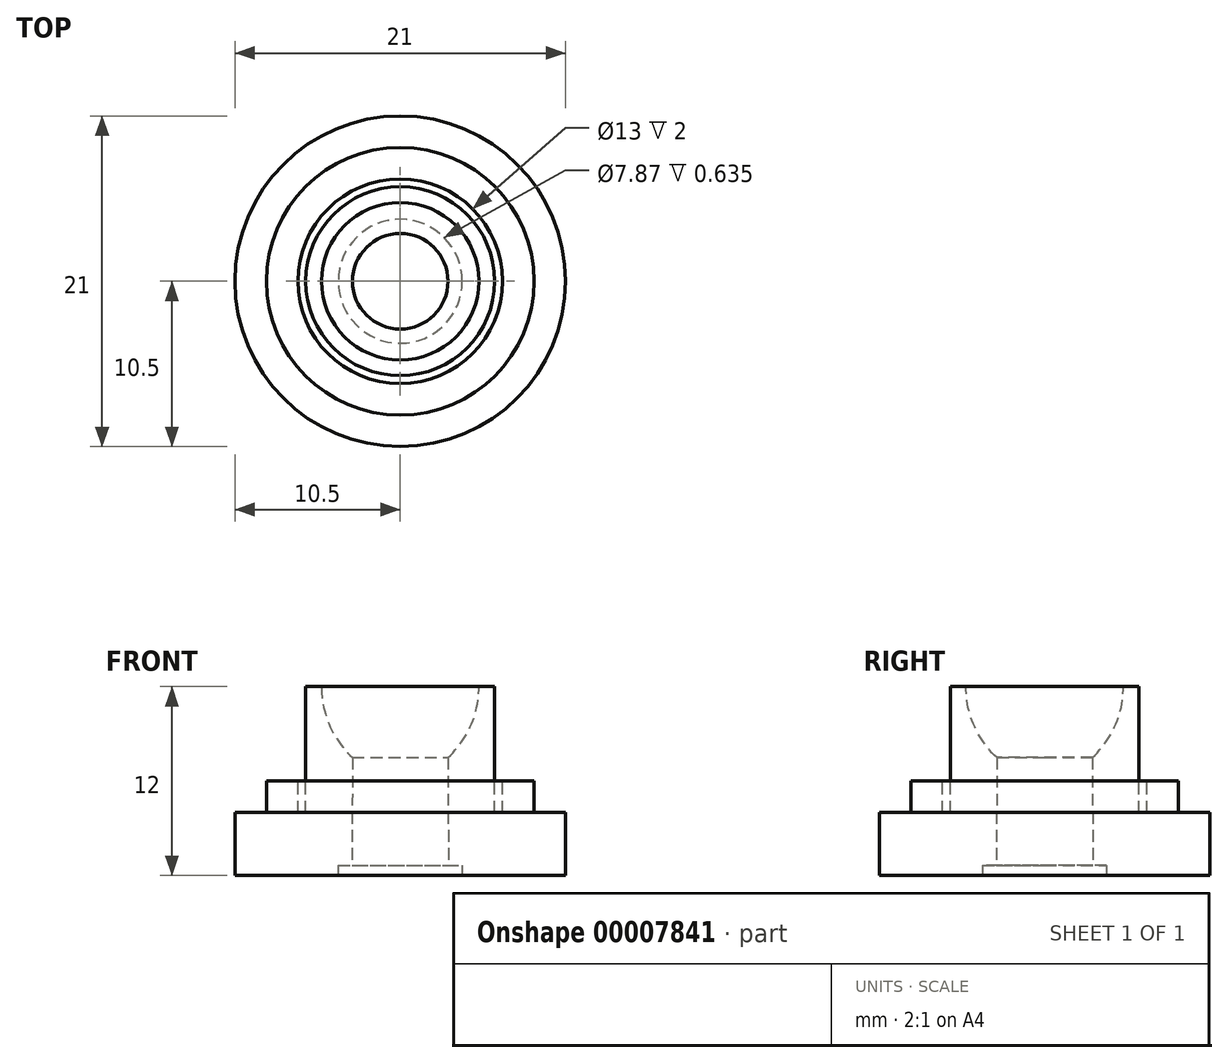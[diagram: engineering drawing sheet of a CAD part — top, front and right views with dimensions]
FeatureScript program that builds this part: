
annotation { "Feature Type Name" : "Feature", "Feature Type Description" : "" }
export const myFeature = defineFeature(function(context is Context, id is Id, definition is map)
    precondition{}
    {
        {
            var Q0;
            Q0=qCreatedBy(makeId("Right.planeOp"),FACE);
            var sketch = newSketch(context, id + "F0", { "sketchPlane" : qUnion([Q0])});
            skLineSegment(sketch, "E0", {"start": v(0, 39.52) * mm, "end": v(0, -33.2) * mm, "construction": true});
            skSolve(sketch);
        }
        {
            var Q0;
            Q0=qCreatedBy(makeId("Right.planeOp"),FACE);
            var sketch = newSketch(context, id + "F1", { "sketchPlane" : qUnion([Q0])});
            skLineSegment(sketch, "E1", {"start": v(0, 0) * mm, "end": v(3.94, 0) * mm});
            skLineSegment(sketch, "E2", {"start": v(3.94, 0) * mm, "end": v(3.94, 0.63) * mm});
            skLineSegment(sketch, "E3", {"start": v(3.94, 0.63) * mm, "end": v(3.06, 0.63) * mm});
            skLineSegment(sketch, "E4", {"start": v(3.06, 0.64) * mm, "end": v(3.04, 7.5) * mm});
            skLineSegment(sketch, "E5", {"start": v(3.04, 7.5) * mm, "end": v(0, 7.5) * mm});
            skLineSegment(sketch, "E6", {"start": v(0, 7.5) * mm, "end": v(0, 0) * mm});
            skSolve(sketch);
        }
        {
            var Q0;
            Q0=qCreatedBy(makeId("Right.planeOp"),FACE);
            var sketch = newSketch(context, id + "F2", { "sketchPlane" : qUnion([Q0])});
            skLineSegment(sketch, "E7.bottom", {"start": v(0, 0) * mm, "end": v(10.5, 0) * mm});
            skLineSegment(sketch, "E7.top", {"start": v(8.5, 4) * mm, "end": v(10.5, 4) * mm});
            skLineSegment(sketch, "E7.right", {"start": v(10.5, 0) * mm, "end": v(10.5, 4) * mm});
            skLineSegment(sketch, "E8", {"start": v(6.5, 6) * mm, "end": v(6.5, 4) * mm});
            skLineSegment(sketch, "E9", {"start": v(6.5, 4) * mm, "end": v(6, 4) * mm});
            skLineSegment(sketch, "E10", {"start": v(6, 4) * mm, "end": v(6, 12) * mm});
            skLineSegment(sketch, "E11", {"start": v(6.5, 6) * mm, "end": v(8.5, 6) * mm});
            skLineSegment(sketch, "E12", {"start": v(8.5, 4) * mm, "end": v(8.5, 6) * mm});
            skLineSegment(sketch, "E13", {"start": v(0, 5.96) * mm, "end": v(0, 0) * mm});
            skLineSegment(sketch, "E14", {"start": v(6, 12) * mm, "end": v(5, 12) * mm});
            skArc(sketch, "E15", {"start": v(0, 5.96) * mm, "mid": v(3.59, 8.08) * mm, "end": v(5, 12) * mm});
            skLineSegment(sketch, "E16", {"start": v(5, 12) * mm, "end": v(-13.8, 12) * mm, "construction": true});
            skPoint(sketch, "E17", {"position": v(-4.4, 12) * mm});
            skSolve(sketch);
        }
        {
            var Q0;
            Q0 = qSketchRegion(id + "F2", true);
            var Q1;
            Q1=sQuery(id+"F0.wireOp",EDGE,"E0");
            revolve(context, id + "F3", {"entities" : qUnion([Q0]), "axis" : qUnion([Q1]), "revolveType" : RevolveType.FULL});
        }
        {
            var Q0;
            Q0 = qSketchRegion(id + "F1", true);
            var Q1;
            Q1=sQuery(id+"F0.wireOp",EDGE,"E0");
            revolve(context, id + "F4", {"operationType" : NewBodyOperationType.REMOVE, "entities" : qUnion([Q0]), "axis" : qUnion([Q1]), "revolveType" : RevolveType.FULL, "oppositeDirection" : true});
        }
    });
